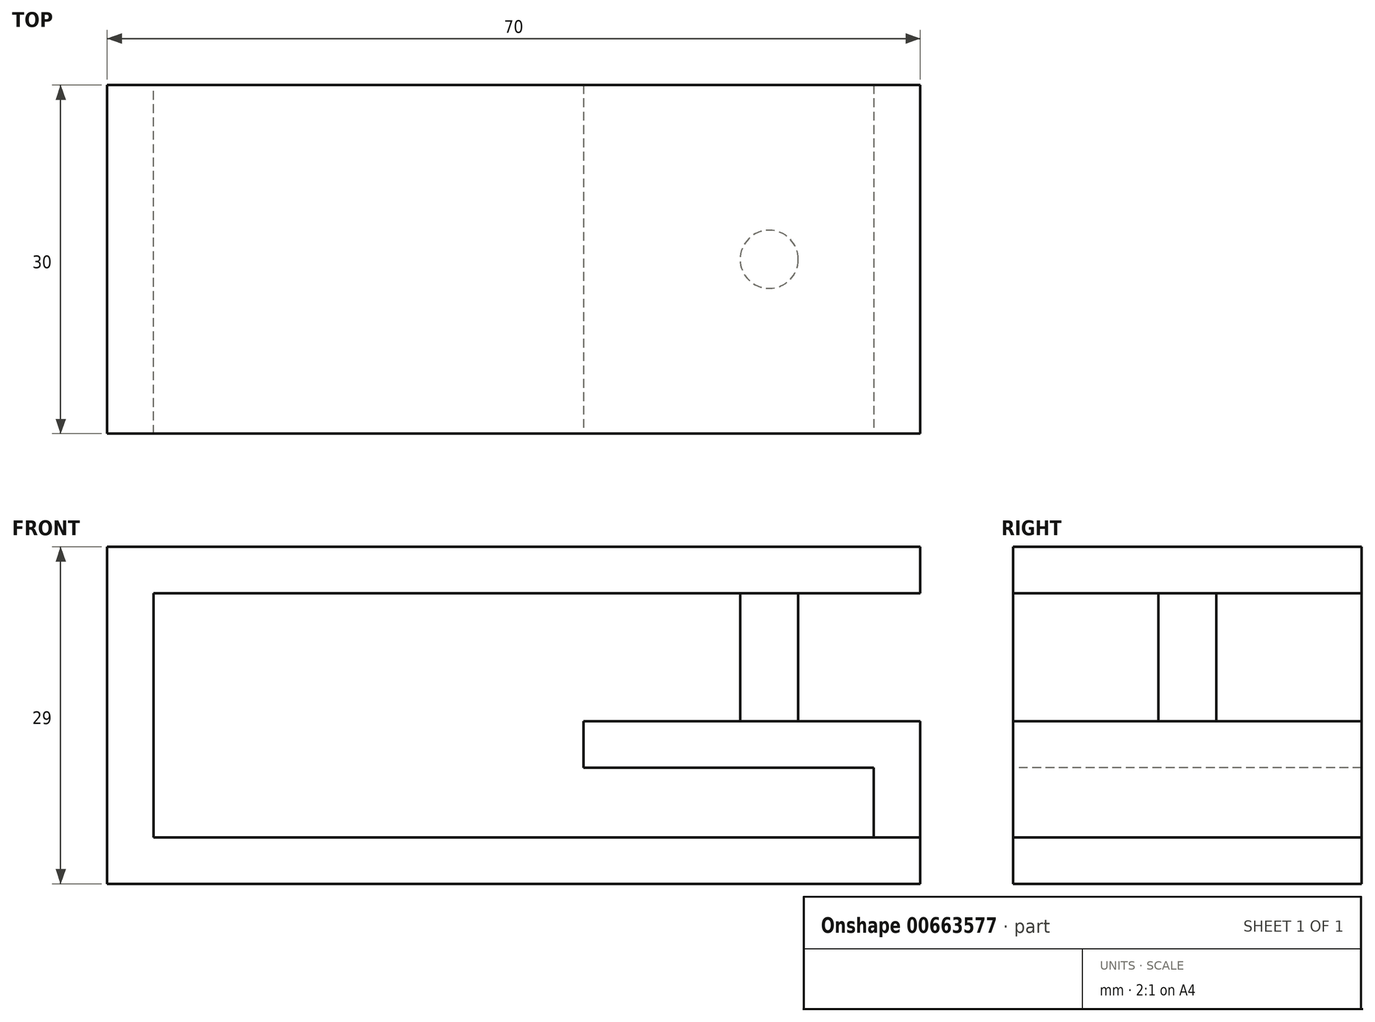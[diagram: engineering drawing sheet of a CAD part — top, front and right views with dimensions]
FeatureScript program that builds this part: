
annotation { "Feature Type Name" : "Feature", "Feature Type Description" : "" }
export const myFeature = defineFeature(function(context is Context, id is Id, definition is map)
    precondition{}
    {
        {
            var Q0;
            Q0=qCreatedBy(makeId("Top.planeOp"),FACE);
            var sketch = newSketch(context, id + "F0", { "sketchPlane" : qUnion([Q0])});
            skLineSegment(sketch, "E0.bottom", {"start": v(0, 0) * mm, "end": v(-70, 0) * mm});
            skLineSegment(sketch, "E0.top", {"start": v(0, 30) * mm, "end": v(-70, 30) * mm});
            skLineSegment(sketch, "E0.left", {"start": v(0, 0) * mm, "end": v(0, 30) * mm});
            skLineSegment(sketch, "E0.right", {"start": v(-70, 0) * mm, "end": v(-70, 30) * mm});
            skSolve(sketch);
        }
        {
            var Q0;
            Q0=makeQuery(id+"F0.imprint","IMPRINT",FACE,{"disambiguationData":[TD([[makeQuery(id+"F0.imprint","IMPRINT",EDGE,{"derivedFrom":sQuery(id+"F0.wireOp",EDGE,"E0.bottom")}),-1.0]])]});
            extrude(context, id + "F1", {"entities" : qUnion([Q0]), "depth" : 4 * mm, "offsetDistance" : 25 * mm});
        }
        {
            var Q0;
            Q0=makeQuery(id+"F1.opExtrude","CAP_FACE",FACE,{"disambiguationData":[OSD([sQuery(id+"F0.wireOp",EDGE,"E0.bottom"),sQuery(id+"F0.wireOp",EDGE,"E0.top"),sQuery(id+"F0.wireOp",EDGE,"E0.left"),sQuery(id+"F0.wireOp",EDGE,"E0.right")])],"isStart":true});
            var sketch = newSketch(context, id + "F2", { "sketchPlane" : qUnion([Q0])});
            skLineSegment(sketch, "E1.bottom", {"start": v(-70, 0) * mm, "end": v(-66, 0) * mm});
            skLineSegment(sketch, "E1.top", {"start": v(-70, -30) * mm, "end": v(-66, -30) * mm});
            skLineSegment(sketch, "E1.left", {"start": v(-70, 0) * mm, "end": v(-70, -30) * mm});
            skLineSegment(sketch, "E1.right", {"start": v(-66, 0) * mm, "end": v(-66, -30) * mm});
            skSolve(sketch);
        }
        {
            var Q0;
            Q0=makeQuery(id+"F2.imprint","IMPRINT",FACE,{"disambiguationData":[TD([[makeQuery(id+"F2.imprint","IMPRINT",EDGE,{"derivedFrom":sQuery(id+"F2.wireOp",EDGE,"E1.bottom")}),1.0]])]});
            extrude(context, id + "F3", {"entities" : qUnion([Q0]), "operationType" : NewBodyOperationType.ADD, "depth" : 25 * mm, "offsetDistance" : 25 * mm});
        }
        {
            var Q0;
            Q0=makeQuery(id+"F3.opExtrude","SWEPT_FACE",FACE,{"disambiguationData":[OSD([sQuery(id+"F2.wireOp",EDGE,"E1.right")])]});
            var sketch = newSketch(context, id + "F4", { "sketchPlane" : qUnion([Q0])});
            skLineSegment(sketch, "E2.bottom", {"start": v(0, -25) * mm, "end": v(30, -25) * mm});
            skLineSegment(sketch, "E2.top", {"start": v(0, -21) * mm, "end": v(30, -21) * mm});
            skLineSegment(sketch, "E2.left", {"start": v(0, -25) * mm, "end": v(0, -21) * mm});
            skLineSegment(sketch, "E2.right", {"start": v(30, -25) * mm, "end": v(30, -21) * mm});
            skSolve(sketch);
        }
        {
            var Q0;
            Q0=makeQuery(id+"F4.imprint","IMPRINT",FACE,{"disambiguationData":[TD([[makeQuery(id+"F4.imprint","IMPRINT",EDGE,{"derivedFrom":sQuery(id+"F4.wireOp",EDGE,"E2.bottom")}),1.0]])]});
            extrude(context, id + "F5", {"entities" : qUnion([Q0]), "operationType" : NewBodyOperationType.ADD, "depth" : 66 * mm, "offsetDistance" : 25 * mm});
        }
        {
            var Q0;
            Q0=makeQuery(id+"F5.opExtrude","SWEPT_FACE",FACE,{"disambiguationData":[OSD([sQuery(id+"F4.wireOp",EDGE,"E2.top")])]});
            var sketch = newSketch(context, id + "F6", { "sketchPlane" : qUnion([Q0])});
            skLineSegment(sketch, "E3.bottom", {"start": v(0, 30) * mm, "end": v(-4, 30) * mm});
            skLineSegment(sketch, "E3.top", {"start": v(0, 0) * mm, "end": v(-4, 0) * mm});
            skLineSegment(sketch, "E3.left", {"start": v(0, 30) * mm, "end": v(0, 0) * mm});
            skLineSegment(sketch, "E3.right", {"start": v(-4, 30) * mm, "end": v(-4, 0) * mm});
            skSolve(sketch);
        }
        {
            var Q0;
            Q0=makeQuery(id+"F6.imprint","IMPRINT",FACE,{"disambiguationData":[TD([[makeQuery(id+"F6.imprint","IMPRINT",EDGE,{"derivedFrom":sQuery(id+"F6.wireOp",EDGE,"E3.bottom")}),1.0]])]});
            extrude(context, id + "F7", {"entities" : qUnion([Q0]), "depth" : 10 * mm, "offsetDistance" : 25 * mm});
        }
        {
            var Q0;
            Q0=makeQuery(id+"F7.opExtrude","SWEPT_FACE",FACE,{"disambiguationData":[OSD([sQuery(id+"F6.wireOp",EDGE,"E3.right")])]});
            var sketch = newSketch(context, id + "F8", { "sketchPlane" : qUnion([Q0])});
            skLineSegment(sketch, "E4.bottom", {"start": v(-30, -11) * mm, "end": v(0, -11) * mm});
            skLineSegment(sketch, "E4.top", {"start": v(-30, -15) * mm, "end": v(0, -15) * mm});
            skLineSegment(sketch, "E4.left", {"start": v(-30, -11) * mm, "end": v(-30, -15) * mm});
            skLineSegment(sketch, "E4.right", {"start": v(0, -11) * mm, "end": v(0, -15) * mm});
            skSolve(sketch);
        }
        {
            var Q0;
            Q0=makeQuery(id+"F8.imprint","IMPRINT",FACE,{"disambiguationData":[TD([[makeQuery(id+"F8.imprint","IMPRINT",EDGE,{"derivedFrom":sQuery(id+"F8.wireOp",EDGE,"E4.bottom")}),-1.0]])]});
            extrude(context, id + "F9", {"entities" : qUnion([Q0]), "operationType" : NewBodyOperationType.ADD, "depth" : 25 * mm, "offsetDistance" : 25 * mm});
        }
        {
            var Q0;
            Q0=makeQuery(id+"F9.boolean.opBoolean","MERGE",FACE,{"derivedFrom":[makeQuery(id+"F7.opExtrude","CAP_FACE",FACE,{"disambiguationData":[OSD([sQuery(id+"F6.wireOp",EDGE,"E3.bottom"),sQuery(id+"F6.wireOp",EDGE,"E3.top"),sQuery(id+"F6.wireOp",EDGE,"E3.left"),sQuery(id+"F6.wireOp",EDGE,"E3.right")])],"isStart":false}),makeQuery(id+"F9.opExtrude","SWEPT_FACE",FACE,{"disambiguationData":[OSD([sQuery(id+"F8.wireOp",EDGE,"E4.bottom")])]})]});
            var sketch = newSketch(context, id + "F10", { "sketchPlane" : qUnion([Q0])});
            skCircle(sketch, "E5", {"center": v(-13, 15) * mm, "radius": 2.5 * mm});
            skPoint(sketch, "E5.centerSnap0", {"position": v(-29, 15) * mm});
            skSolve(sketch);
        }
        {
            var Q0;
            Q0=makeQuery(id+"F10.imprint","IMPRINT",FACE,{"disambiguationData":[TD([[makeQuery(id+"F10.imprint","IMPRINT",EDGE,{"derivedFrom":sQuery(id+"F10.wireOp",EDGE,"E5")}),1.0]])]});
            extrude(context, id + "F11", {"entities" : qUnion([Q0]), "depth" : 11 * mm, "offsetDistance" : 25 * mm});
        }
    });
